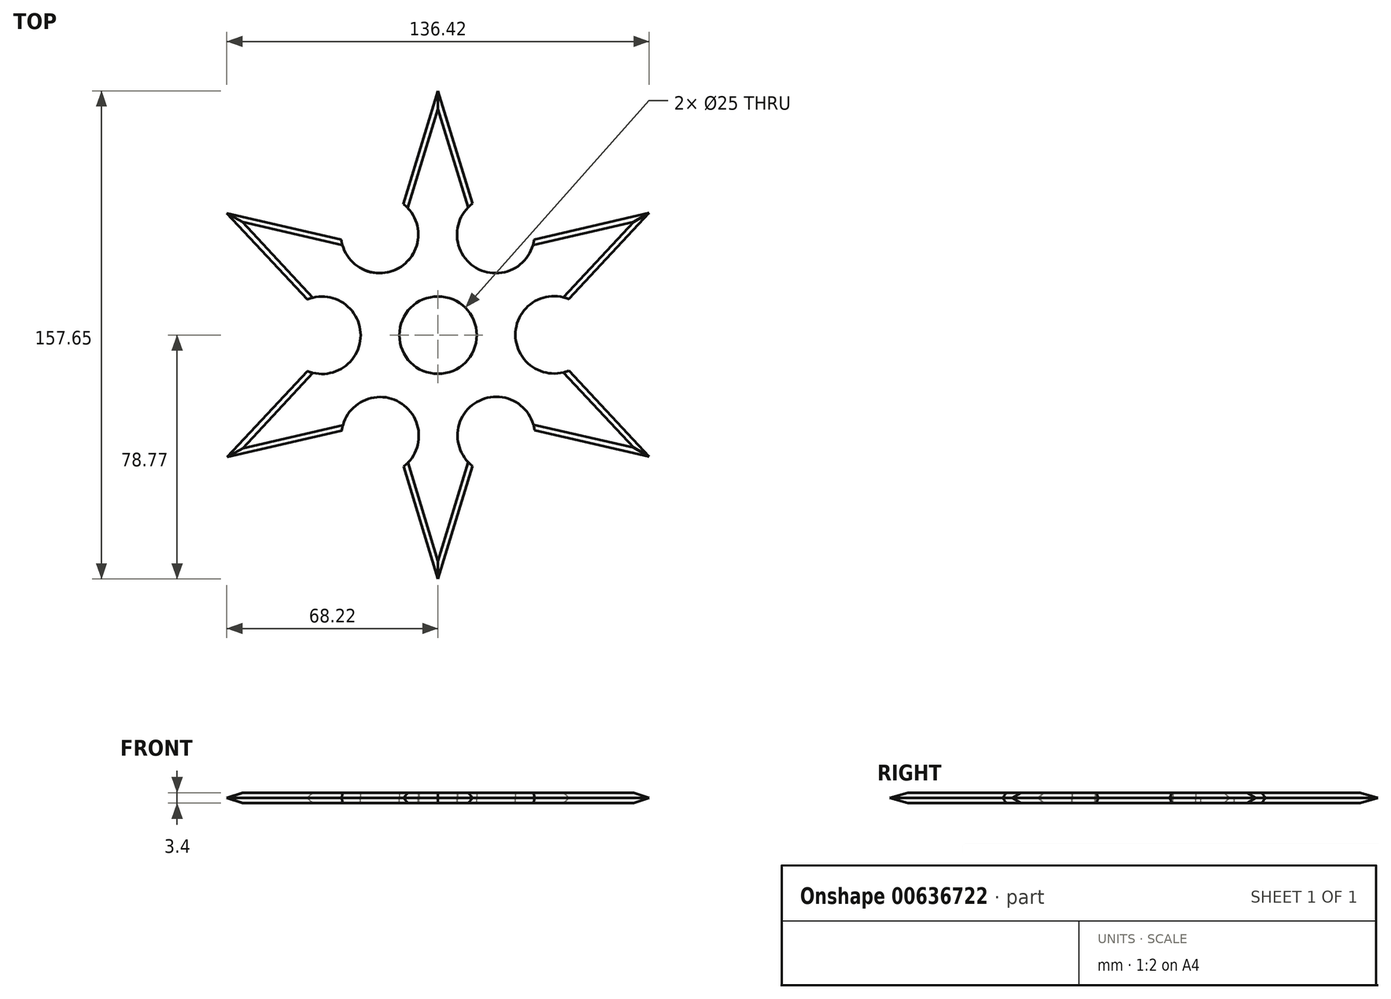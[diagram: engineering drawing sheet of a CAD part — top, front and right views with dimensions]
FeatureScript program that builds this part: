
annotation { "Feature Type Name" : "Feature", "Feature Type Description" : "" }
export const myFeature = defineFeature(function(context is Context, id is Id, definition is map)
    precondition{}
    {
        {
            var Q0;
            Q0=qCreatedBy(makeId("Top.planeOp"),FACE);
            var sketch = newSketch(context, id + "F0", { "sketchPlane" : qUnion([Q0])});
            skCircle(sketch, "E0", {"center": v(0, 0) * mm, "radius": 12.5 * mm});
            skArc(sketch, "E1", {"start": v(-25.07, 21.68) * mm, "mid": v(-12.62, 21.72) * mm, "end": v(-6.4, 32.5) * mm});
            skArc(sketch, "E2", {"start": v(-43.56, -10.97) * mm, "mid": v(-26.61, -6.17) * mm, "end": v(-31.3, 10.81) * mm});
            skPoint(sketch, "E3.end.orphan", {"position": v(0, -66.44) * mm});
            skPoint(sketch, "E4", {"position": v(43.3, -25) * mm});
            skPoint(sketch, "E5", {"position": v(43.3, 25) * mm});
            skPoint(sketch, "E6", {"position": v(0, 50) * mm});
            skPoint(sketch, "E7", {"position": v(-43.28, 24.96) * mm});
            skPoint(sketch, "E8", {"position": v(-43.3, -25) * mm});
            skLineSegment(sketch, "E9", {"start": v(-12.24, -43.18) * mm, "end": v(0, -83.22) * mm});
            skPoint(sketch, "E10.orphan", {"position": v(0.04, -43.18) * mm});
            skLineSegment(sketch, "E11", {"start": v(0, 0) * mm, "end": v(0, -0.17) * mm});
            skArc(sketch, "E12", {"start": v(31.29, -32.09) * mm, "mid": v(12.54, -21.58) * mm, "end": v(12.27, -43.07) * mm});
            skArc(sketch, "E13", {"start": v(-12.24, -43.18) * mm, "mid": v(-12.46, -21.66) * mm, "end": v(-31.2, -32.23) * mm});
            skArc(sketch, "E14", {"start": v(-43.56, -10.97) * mm, "mid": v(-25, -0.1) * mm, "end": v(-43.45, 10.96) * mm});
            skArc(sketch, "E15", {"start": v(-31.37, 32.25) * mm, "mid": v(-12.68, 21.65) * mm, "end": v(-12.3, 43.14) * mm});
            skArc(sketch, "E16", {"start": v(12.24, 43.25) * mm, "mid": v(12.34, 21.7) * mm, "end": v(31.12, 32.27) * mm});
            skArc(sketch, "E17", {"start": v(43.48, 11.07) * mm, "mid": v(24.99, 0.1) * mm, "end": v(43.49, -10.87) * mm});
            skLineSegment(sketch, "E18", {"start": v(72.05, -41.5) * mm, "end": v(31.29, -32.09) * mm});
            skLineSegment(sketch, "E19", {"start": v(-0.01, 0.1) * mm, "end": v(-0.01, 0.23) * mm});
            skLineSegment(sketch, "E20", {"start": v(0, 0.04) * mm, "end": v(0.06, -0.07) * mm});
            skLineSegment(sketch, "E21", {"start": v(0.08, -0.03) * mm, "end": v(0, -0.17) * mm});
            skLineSegment(sketch, "E22", {"start": v(-25.07, 21.68) * mm, "end": v(-25.09, 21.66) * mm});
            skLineSegment(sketch, "E23", {"start": v(-0.13, 0.04) * mm, "end": v(0, 0.04) * mm});
            skLineSegment(sketch, "E24", {"start": v(-12.64, 21.7) * mm, "end": v(-12.63, 21.68) * mm});
            skLineSegment(sketch, "E25", {"start": v(-0.01, 0.23) * mm, "end": v(-0.13, 0.03) * mm});
            skLineSegment(sketch, "E26", {"start": v(0, 0.04) * mm, "end": v(-0.2, 0.15) * mm});
            skLineSegment(sketch, "E27", {"start": v(-72.07, 41.65) * mm, "end": v(-31.37, 32.25) * mm});
            skLineSegment(sketch, "E28", {"start": v(0.08, -0.03) * mm, "end": v(0, -0.08) * mm});
            skLineSegment(sketch, "E29", {"start": v(-71.99, -41.64) * mm, "end": v(-43.44, -11.03) * mm});
            skLineSegment(sketch, "E30", {"start": v(-71.99, -41.64) * mm, "end": v(-31.2, -32.23) * mm});
            skPoint(sketch, "E31", {"position": v(-43.45, 10.96) * mm});
            skLineSegment(sketch, "E32", {"start": v(-72.07, 41.65) * mm, "end": v(-43.45, 10.96) * mm});
            skPoint(sketch, "E33", {"position": v(-12.3, 43.14) * mm});
            skLineSegment(sketch, "E34", {"start": v(-12.3, 43.14) * mm, "end": v(-0.01, 83.32) * mm});
            skPoint(sketch, "E35", {"position": v(12.24, 43.25) * mm});
            skLineSegment(sketch, "E36", {"start": v(12.24, 43.25) * mm, "end": v(-0.01, 83.32) * mm});
            skPoint(sketch, "E37", {"position": v(31.12, 32.27) * mm});
            skLineSegment(sketch, "E38", {"start": v(31.12, 32.27) * mm, "end": v(72.05, 41.72) * mm});
            skPoint(sketch, "E39", {"position": v(43.48, 11.07) * mm});
            skLineSegment(sketch, "E40", {"start": v(43.48, 11.07) * mm, "end": v(72.05, 41.72) * mm});
            skPoint(sketch, "E41", {"position": v(43.49, -10.87) * mm});
            skLineSegment(sketch, "E42", {"start": v(43.49, -10.87) * mm, "end": v(72.05, -41.5) * mm});
            skPoint(sketch, "E43", {"position": v(12.27, -43.07) * mm});
            skPoint(sketch, "E44.start.orphan", {"position": v(12.24, -43.18) * mm});
            skLineSegment(sketch, "E45", {"start": v(12.27, -43.07) * mm, "end": v(0, -83.22) * mm});
            skLineSegment(sketch, "E46.trimOffspring", {"start": v(-6.38, 32.5) * mm, "end": v(-6.4, 32.5) * mm});
            skLineSegment(sketch, "E47.trimOffspring", {"start": v(-0.2, 0.15) * mm, "end": v(-0.13, 0.03) * mm});
            skSolve(sketch);
        }
        {
            var Q0;
            Q0=makeQuery(id+"F0.imprint","IMPRINT",FACE,{"disambiguationData":[TD([[makeQuery(id+"F0.imprint","IMPRINT",EDGE,{"derivedFrom":sQuery(id+"F0.wireOp",EDGE,"E0")}),-1.0]])]});
            extrude(context, id + "F1", {"entities" : qUnion([Q0]), "depth" : 1.7 * mm, "offsetDistance" : 25 * mm});
        }
        {
            var Q0;
            Q0=makeQuery(id+"F1.opExtrude","CAP_EDGE",EDGE,{"disambiguationData":[OSD([sQuery(id+"F0.wireOp",EDGE,"E32")])],"isStart":false});
            var Q1;
            Q1=makeQuery(id+"F1.opExtrude","CAP_EDGE",EDGE,{"disambiguationData":[OSD([sQuery(id+"F0.wireOp",EDGE,"E27")])],"isStart":false});
            var Q2;
            Q2=makeQuery(id+"F1.opExtrude","CAP_EDGE",EDGE,{"disambiguationData":[OSD([sQuery(id+"F0.wireOp",EDGE,"E34")])],"isStart":false});
            var Q3;
            Q3=makeQuery(id+"F1.opExtrude","CAP_EDGE",EDGE,{"disambiguationData":[OSD([sQuery(id+"F0.wireOp",EDGE,"E36")])],"isStart":false});
            var Q4;
            Q4=makeQuery(id+"F1.opExtrude","CAP_EDGE",EDGE,{"disambiguationData":[OSD([sQuery(id+"F0.wireOp",EDGE,"E38")])],"isStart":false});
            var Q5;
            Q5=makeQuery(id+"F1.opExtrude","CAP_EDGE",EDGE,{"disambiguationData":[OSD([sQuery(id+"F0.wireOp",EDGE,"E40")])],"isStart":false});
            var Q6;
            Q6=makeQuery(id+"F1.opExtrude","CAP_EDGE",EDGE,{"disambiguationData":[OSD([sQuery(id+"F0.wireOp",EDGE,"E42")])],"isStart":false});
            var Q7;
            Q7=makeQuery(id+"F1.opExtrude","CAP_EDGE",EDGE,{"disambiguationData":[OSD([sQuery(id+"F0.wireOp",EDGE,"E18")])],"isStart":false});
            var Q8;
            Q8=makeQuery(id+"F1.opExtrude","CAP_EDGE",EDGE,{"disambiguationData":[OSD([sQuery(id+"F0.wireOp",EDGE,"E45")])],"isStart":false});
            var Q9;
            Q9=makeQuery(id+"F1.opExtrude","CAP_EDGE",EDGE,{"disambiguationData":[OSD([sQuery(id+"F0.wireOp",EDGE,"E9")])],"isStart":false});
            var Q10;
            Q10=makeQuery(id+"F1.opExtrude","CAP_EDGE",EDGE,{"disambiguationData":[OSD([sQuery(id+"F0.wireOp",EDGE,"E29")])],"isStart":false});
            var Q11;
            Q11=makeQuery(id+"F1.opExtrude","CAP_EDGE",EDGE,{"disambiguationData":[OSD([sQuery(id+"F0.wireOp",EDGE,"E30")])],"isStart":false});
            chamfer(context, id + "F2", {"entities" : qUnion([Q0, Q1, Q2, Q3, Q4, Q5, Q6, Q7, Q8, Q9, Q10, Q11]), "width" : 3 * mm, "tangentPropagation" : true});
        }
        {
            var Q0;
            Q0 = qSketchRegion(id + "F0", true);
            extrude(context, id + "F3", {"entities" : qUnion([Q0]), "oppositeDirection" : true, "depth" : 1.7 * mm, "offsetDistance" : 25 * mm});
        }
        {
            var Q0;
            Q0=makeQuery(id+"F3.opExtrude","CAP_EDGE",EDGE,{"disambiguationData":[OSD([sQuery(id+"F0.wireOp",EDGE,"E45")])],"isStart":false});
            var Q1;
            Q1=makeQuery(id+"F3.opExtrude","CAP_EDGE",EDGE,{"disambiguationData":[OSD([sQuery(id+"F0.wireOp",EDGE,"E9")])],"isStart":false});
            var Q2;
            Q2=makeQuery(id+"F3.opExtrude","CAP_EDGE",EDGE,{"disambiguationData":[OSD([sQuery(id+"F0.wireOp",EDGE,"E18")])],"isStart":false});
            var Q3;
            Q3=makeQuery(id+"F3.opExtrude","CAP_EDGE",EDGE,{"disambiguationData":[OSD([sQuery(id+"F0.wireOp",EDGE,"E42")])],"isStart":false});
            var Q4;
            Q4=makeQuery(id+"F3.opExtrude","CAP_EDGE",EDGE,{"disambiguationData":[OSD([sQuery(id+"F0.wireOp",EDGE,"E40")])],"isStart":false});
            var Q5;
            Q5=makeQuery(id+"F3.opExtrude","CAP_EDGE",EDGE,{"disambiguationData":[OSD([sQuery(id+"F0.wireOp",EDGE,"E38")])],"isStart":false});
            var Q6;
            Q6=makeQuery(id+"F3.opExtrude","CAP_EDGE",EDGE,{"disambiguationData":[OSD([sQuery(id+"F0.wireOp",EDGE,"E36")])],"isStart":false});
            var Q7;
            Q7=makeQuery(id+"F3.opExtrude","CAP_EDGE",EDGE,{"disambiguationData":[OSD([sQuery(id+"F0.wireOp",EDGE,"E34")])],"isStart":false});
            var Q8;
            Q8=makeQuery(id+"F3.opExtrude","CAP_EDGE",EDGE,{"disambiguationData":[OSD([sQuery(id+"F0.wireOp",EDGE,"E27")])],"isStart":false});
            var Q9;
            Q9=makeQuery(id+"F3.opExtrude","CAP_EDGE",EDGE,{"disambiguationData":[OSD([sQuery(id+"F0.wireOp",EDGE,"E32")])],"isStart":false});
            var Q10;
            Q10=makeQuery(id+"F3.opExtrude","CAP_EDGE",EDGE,{"disambiguationData":[OSD([sQuery(id+"F0.wireOp",EDGE,"E29")])],"isStart":false});
            var Q11;
            Q11=makeQuery(id+"F3.opExtrude","CAP_EDGE",EDGE,{"disambiguationData":[OSD([sQuery(id+"F0.wireOp",EDGE,"E30")])],"isStart":false});
            chamfer(context, id + "F4", {"entities" : qUnion([Q0, Q1, Q2, Q3, Q4, Q5, Q6, Q7, Q8, Q9, Q10, Q11]), "width" : 3 * mm, "tangentPropagation" : true});
        }
    });
